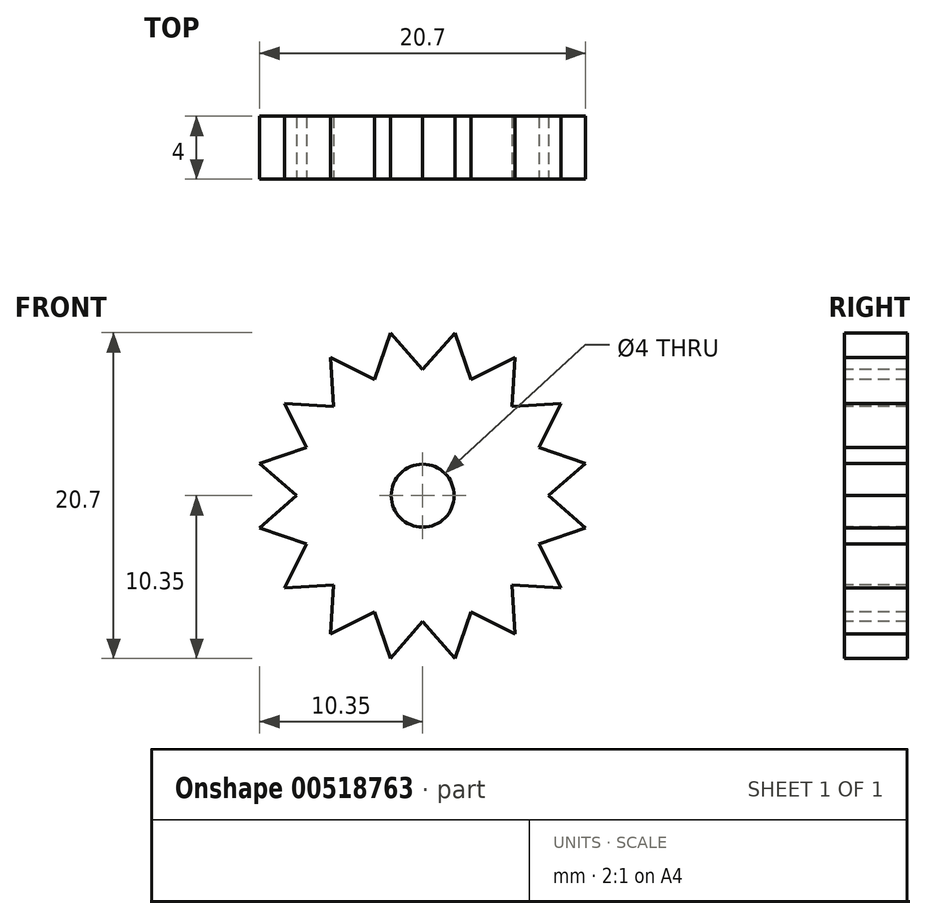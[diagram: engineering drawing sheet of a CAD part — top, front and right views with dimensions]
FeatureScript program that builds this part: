
annotation { "Feature Type Name" : "Feature", "Feature Type Description" : "" }
export const myFeature = defineFeature(function(context is Context, id is Id, definition is map)
    precondition{}
    {
        {
            var Q0;
            Q0=qCreatedBy(makeId("Front.planeOp"),FACE);
            var sketch = newSketch(context, id + "F0", { "sketchPlane" : qUnion([Q0])});
            skCircle(sketch, "E0", {"center": v(0, 0) * mm, "radius": 8 * mm});
            skLineSegment(sketch, "E1", {"start": v(-2.06, 10.35) * mm, "end": v(-3.06, 7.4) * mm});
            skCircle(sketch, "E2", {"center": v(0, 0) * mm, "radius": 2 * mm});
            skLineSegment(sketch, "E3", {"start": v(0, 0) * mm, "end": v(-3.06, 7.4) * mm, "construction": true});
            skLineSegment(sketch, "E4", {"start": v(-2.06, 10.35) * mm, "end": v(0, 8) * mm});
            skLineSegment(sketch, "E5.1.0", {"start": v(-5.86, 8.77) * mm, "end": v(-3.06, 7.4) * mm});
            skLineSegment(sketch, "E5.1.1", {"start": v(-5.86, 8.77) * mm, "end": v(-5.66, 5.66) * mm});
            skLineSegment(sketch, "E5.2.0", {"start": v(-8.77, 5.86) * mm, "end": v(-5.66, 5.66) * mm});
            skLineSegment(sketch, "E5.2.1", {"start": v(-8.77, 5.86) * mm, "end": v(-7.4, 3.06) * mm});
            skLineSegment(sketch, "E5.3.0", {"start": v(-10.35, 2.06) * mm, "end": v(-7.4, 3.06) * mm});
            skLineSegment(sketch, "E5.3.1", {"start": v(-10.35, 2.06) * mm, "end": v(-8, 0) * mm});
            skLineSegment(sketch, "E5.4.0", {"start": v(-10.35, -2.06) * mm, "end": v(-8, 0) * mm});
            skLineSegment(sketch, "E5.4.1", {"start": v(-10.35, -2.06) * mm, "end": v(-7.4, -3.06) * mm});
            skLineSegment(sketch, "E5.5.0", {"start": v(-8.77, -5.86) * mm, "end": v(-7.4, -3.06) * mm});
            skLineSegment(sketch, "E5.5.1", {"start": v(-8.77, -5.86) * mm, "end": v(-5.66, -5.66) * mm});
            skLineSegment(sketch, "E5.6.0", {"start": v(-5.86, -8.77) * mm, "end": v(-5.66, -5.66) * mm});
            skLineSegment(sketch, "E5.6.1", {"start": v(-5.86, -8.77) * mm, "end": v(-3.06, -7.4) * mm});
            skLineSegment(sketch, "E5.7.0", {"start": v(-2.06, -10.35) * mm, "end": v(-3.06, -7.4) * mm});
            skLineSegment(sketch, "E5.7.1", {"start": v(-2.06, -10.35) * mm, "end": v(0, -8) * mm});
            skLineSegment(sketch, "E5.8.0", {"start": v(2.06, -10.35) * mm, "end": v(0, -8) * mm});
            skLineSegment(sketch, "E5.8.1", {"start": v(2.06, -10.35) * mm, "end": v(3.06, -7.4) * mm});
            skLineSegment(sketch, "E5.9.0", {"start": v(5.86, -8.77) * mm, "end": v(3.06, -7.4) * mm});
            skLineSegment(sketch, "E5.9.1", {"start": v(5.86, -8.77) * mm, "end": v(5.66, -5.66) * mm});
            skLineSegment(sketch, "E5.10.0", {"start": v(8.77, -5.86) * mm, "end": v(5.66, -5.66) * mm});
            skLineSegment(sketch, "E5.10.1", {"start": v(8.77, -5.86) * mm, "end": v(7.4, -3.06) * mm});
            skLineSegment(sketch, "E5.11.0", {"start": v(10.35, -2.06) * mm, "end": v(7.4, -3.06) * mm});
            skLineSegment(sketch, "E5.11.1", {"start": v(10.35, -2.06) * mm, "end": v(8, 0) * mm});
            skLineSegment(sketch, "E5.12.0", {"start": v(10.35, 2.06) * mm, "end": v(8, 0) * mm});
            skLineSegment(sketch, "E5.12.1", {"start": v(10.35, 2.06) * mm, "end": v(7.4, 3.06) * mm});
            skLineSegment(sketch, "E5.13.0", {"start": v(8.77, 5.86) * mm, "end": v(7.4, 3.06) * mm});
            skLineSegment(sketch, "E5.13.1", {"start": v(8.77, 5.86) * mm, "end": v(5.66, 5.66) * mm});
            skLineSegment(sketch, "E5.14.0", {"start": v(5.86, 8.77) * mm, "end": v(5.66, 5.66) * mm});
            skLineSegment(sketch, "E5.14.1", {"start": v(5.86, 8.77) * mm, "end": v(3.06, 7.4) * mm});
            skLineSegment(sketch, "E5.15.0", {"start": v(2.06, 10.35) * mm, "end": v(3.06, 7.4) * mm});
            skLineSegment(sketch, "E5.15.1", {"start": v(2.06, 10.35) * mm, "end": v(0, 8) * mm});
            skSolve(sketch);
        }
        {
            var Q0;
            Q0=qSketchRegion(id+"F0",true);
            extrude(context, id + "F1", {"entities" : qUnion([Q0]), "endBound" : BoundingType.SYMMETRIC, "oppositeDirection" : true, "depth" : 4 * mm, "offsetDistance" : 25 * mm});
        }
    });
